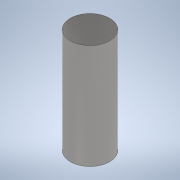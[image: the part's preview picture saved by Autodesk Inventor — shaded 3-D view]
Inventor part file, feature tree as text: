
AUTODESK INVENTOR PART (.ipt)
format: ipt  version: 2020 (Build 240168000, 168)  size: 92,160 bytes
history: native  units: mm
features: extrude x1, sketch x1
ambient origin geometry x8: Origin, YZ Plane, XZ Plane, XY Plane, X Axis, Y Axis, Z Axis, Center Point
bodies: Solid1 (feature_tree)
feature tree (2):
  extrude  "Extrusion1"  Depth=4.0mm TaperAngle=0.0deg
  sketch  "Sketch1"  dims[d0=1.5mm d1=4.0mm d2=0.0mm]
